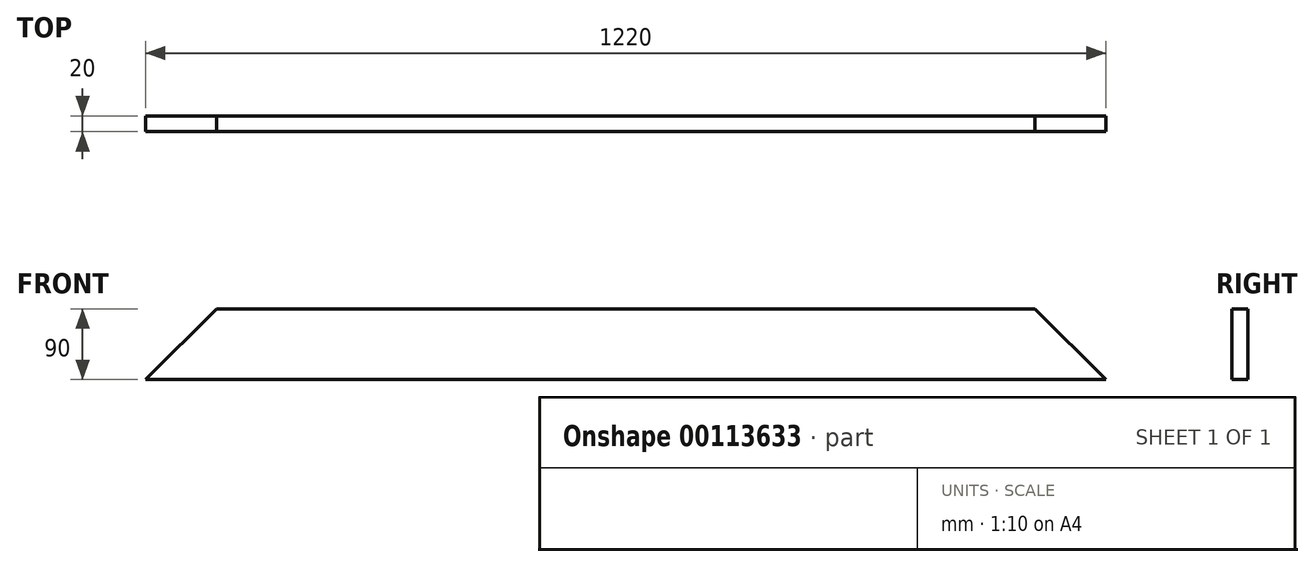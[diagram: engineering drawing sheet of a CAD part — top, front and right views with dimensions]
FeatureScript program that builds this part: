
annotation { "Feature Type Name" : "Feature", "Feature Type Description" : "" }
export const myFeature = defineFeature(function(context is Context, id is Id, definition is map)
    precondition{}
    {
        {
            var Q0;
            Q0=qCreatedBy(makeId("Front.planeOp"),FACE);
            var sketch = newSketch(context, id + "F0", { "sketchPlane" : qUnion([Q0])});
            skLineSegment(sketch, "E0.bottom", {"start": v(-500, 0) * mm, "end": v(720, 0) * mm});
            skLineSegment(sketch, "E0.top", {"start": v(-410, 90) * mm, "end": v(630, 90) * mm});
            skLineSegment(sketch, "E1", {"start": v(-500, 0) * mm, "end": v(-410, 90) * mm});
            skLineSegment(sketch, "E2", {"start": v(720, 0) * mm, "end": v(630, 90) * mm});
            skSolve(sketch);
        }
        {
            var Q0;
            Q0=makeQuery(id+"F0.imprint","IMPRINT",FACE,{"disambiguationData":[TD([[makeQuery(id+"F0.imprint","IMPRINT",EDGE,{"derivedFrom":sQuery(id+"F0.wireOp",EDGE,"E0.bottom")}),1.0]])]});
            extrude(context, id + "F1", {"entities" : qUnion([Q0]), "depth" : 20 * mm});
        }
    });
